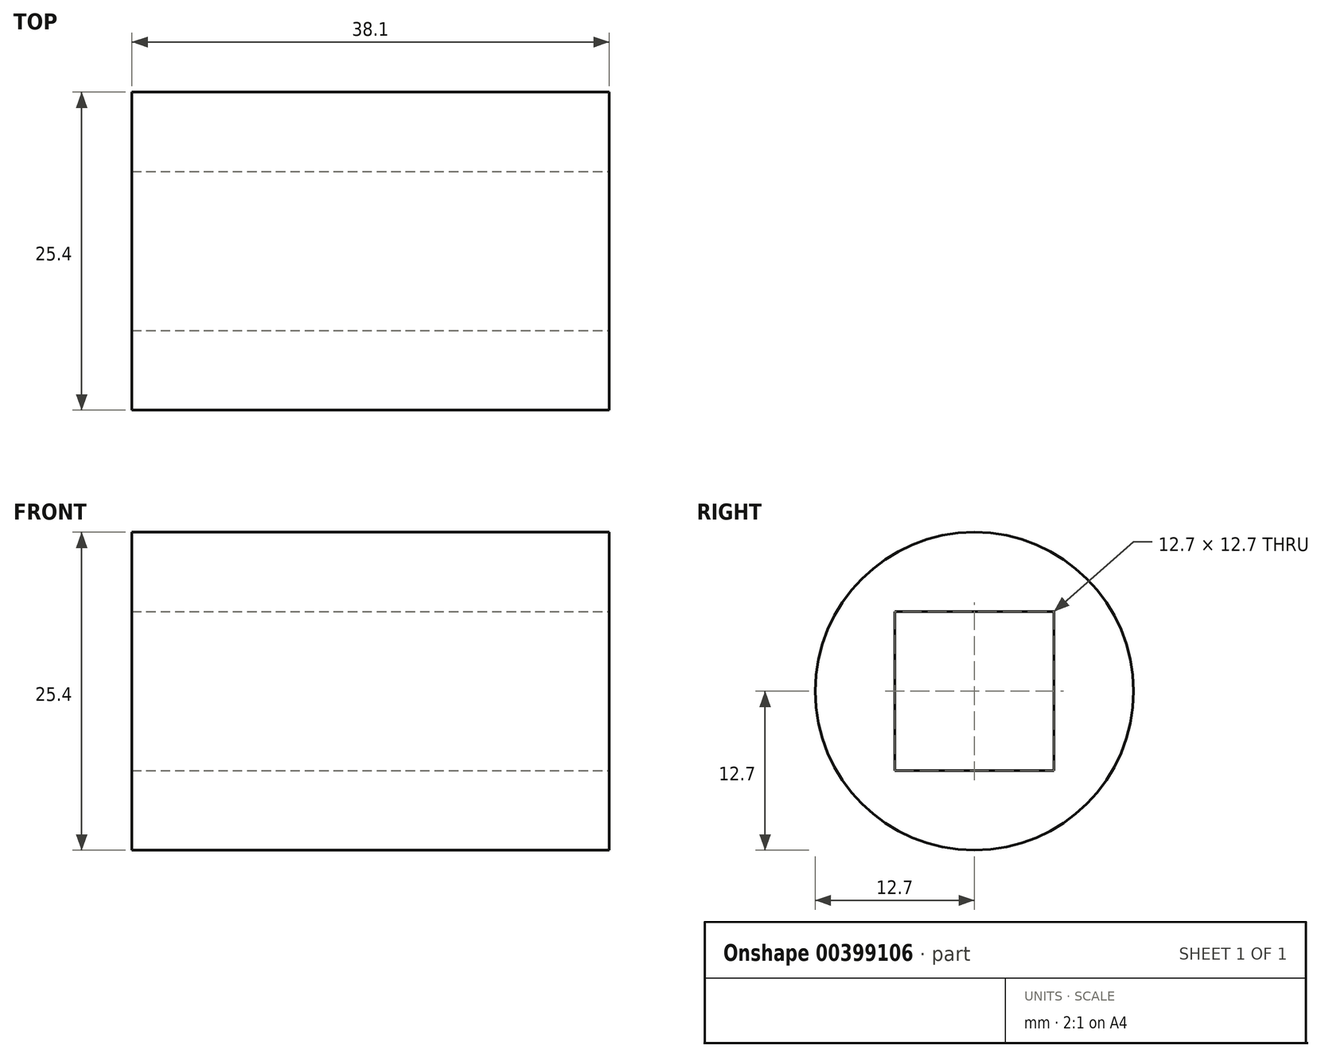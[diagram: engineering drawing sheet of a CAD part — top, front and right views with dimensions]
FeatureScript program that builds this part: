
annotation { "Feature Type Name" : "Feature", "Feature Type Description" : "" }
export const myFeature = defineFeature(function(context is Context, id is Id, definition is map)
    precondition{}
    {
        {
            var Q0;
            Q0=qCreatedBy(makeId("Right.planeOp"),FACE);
            var sketch = newSketch(context, id + "F0", { "sketchPlane" : qUnion([Q0])});
            skCircle(sketch, "E0", {"center": v(0, 0) * mm, "radius": 12.7 * mm});
            skSolve(sketch);
        }
        {
            var Q0;
            Q0=makeQuery(id+"F0.imprint","IMPRINT",FACE,{"disambiguationData":[TD([[makeQuery(id+"F0.imprint","IMPRINT",EDGE,{"derivedFrom":sQuery(id+"F0.wireOp",EDGE,"E0")}),1.0]])]});
            extrude(context, id + "F1", {"entities" : qUnion([Q0]), "depth" : 38.1 * mm});
        }
        {
            var Q0;
            Q0=makeQuery(id+"F1.opExtrude","CAP_FACE",FACE,{"disambiguationData":[OSD([sQuery(id+"F0.wireOp",EDGE,"E0")])],"isStart":false});
            var sketch = newSketch(context, id + "F2", { "sketchPlane" : qUnion([Q0])});
            skLineSegment(sketch, "E1.bottom", {"start": v(-6.35, -6.35) * mm, "end": v(6.35, -6.35) * mm});
            skLineSegment(sketch, "E1.top", {"start": v(-6.35, 6.35) * mm, "end": v(6.35, 6.35) * mm});
            skLineSegment(sketch, "E1.left", {"start": v(-6.35, -6.35) * mm, "end": v(-6.35, 6.35) * mm});
            skLineSegment(sketch, "E1.right", {"start": v(6.35, -6.35) * mm, "end": v(6.35, 6.35) * mm});
            skPoint(sketch, "E1.middle", {"position": v(0, 0) * mm});
            skSolve(sketch);
        }
        {
            var Q0;
            Q0=makeQuery(id+"F2.imprint","IMPRINT",FACE,{"disambiguationData":[TD([[makeQuery(id+"F2.imprint","IMPRINT",EDGE,{"derivedFrom":sQuery(id+"F2.wireOp",EDGE,"E1.bottom")}),1.0]])]});
            extrude(context, id + "F3", {"entities" : qUnion([Q0]), "operationType" : NewBodyOperationType.REMOVE, "oppositeDirection" : true, "depth" : 38.1 * mm});
        }
    });
